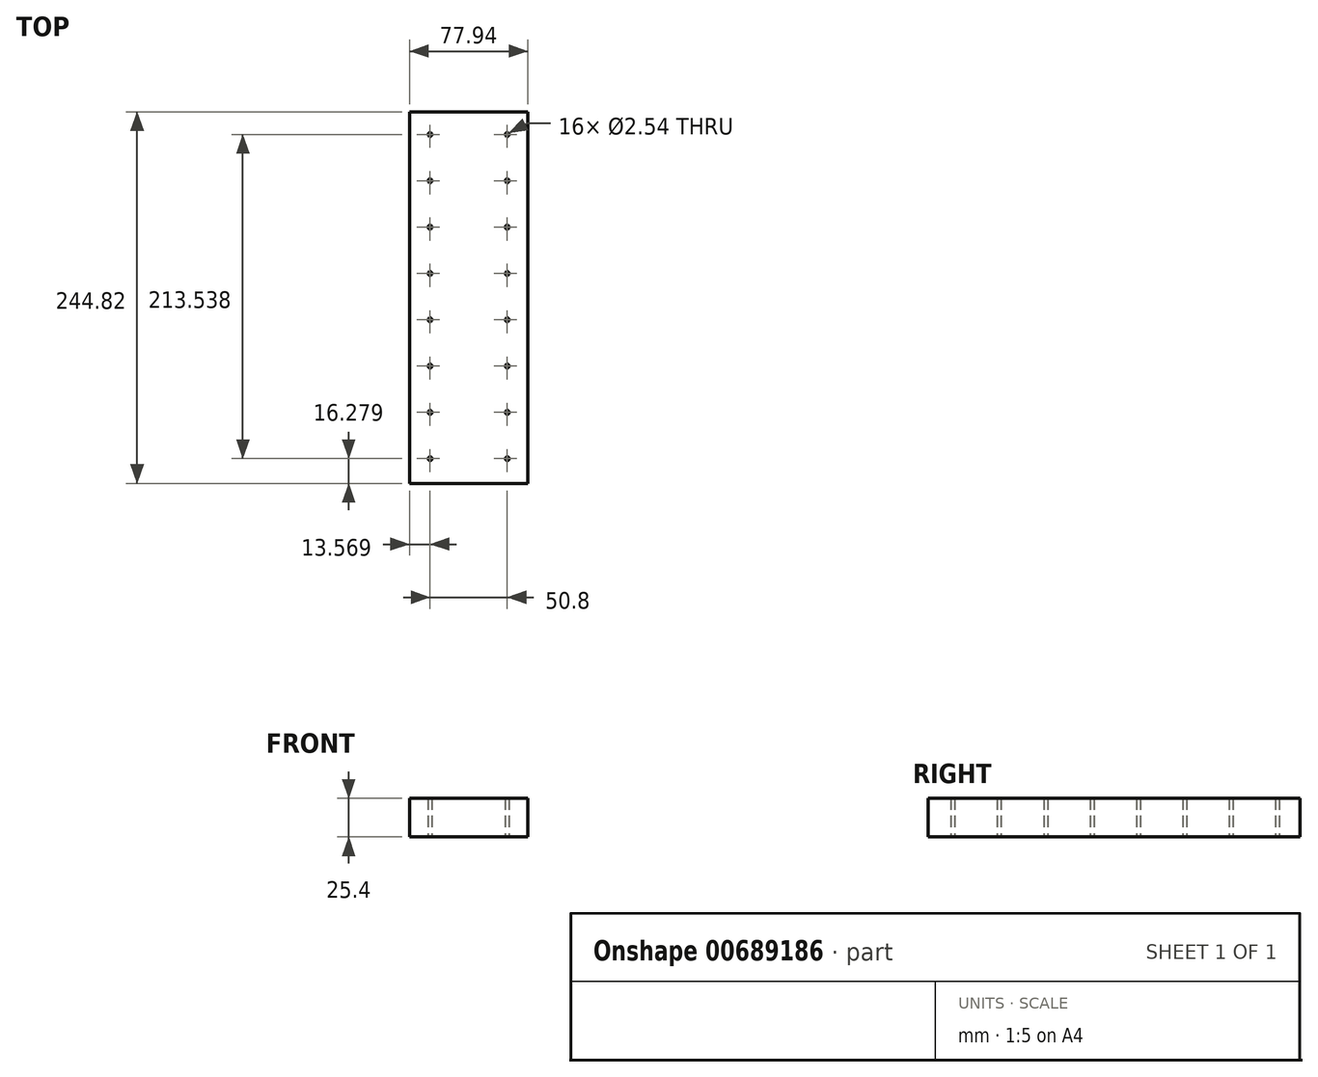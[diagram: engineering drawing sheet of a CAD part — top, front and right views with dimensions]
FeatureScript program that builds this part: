
annotation { "Feature Type Name" : "Feature", "Feature Type Description" : "" }
export const myFeature = defineFeature(function(context is Context, id is Id, definition is map)
    precondition{}
    {
        {
            var Q0;
            Q0=qCreatedBy(makeId("Top.planeOp"),FACE);
            var sketch = newSketch(context, id + "F0", { "sketchPlane" : qUnion([Q0])});
            skLineSegment(sketch, "E0", {"start": v(-47.84, 27.19) * mm, "end": v(2.96, 27.19) * mm, "construction": true});
            skCircle(sketch, "E1", {"center": v(-47.84, 27.19) * mm, "radius": 1.27 * mm});
            skCircle(sketch, "E2", {"center": v(2.96, 27.19) * mm, "radius": 1.27 * mm});
            skLineSegment(sketch, "E3.0.1.0", {"start": v(-47.84, -3.32) * mm, "end": v(2.96, -3.32) * mm, "construction": true});
            skCircle(sketch, "E3.0.1.1", {"center": v(-47.84, -3.32) * mm, "radius": 1.27 * mm});
            skCircle(sketch, "E3.0.1.2", {"center": v(2.96, -3.32) * mm, "radius": 1.27 * mm});
            skLineSegment(sketch, "E3.0.2.0", {"start": v(-47.84, -33.82) * mm, "end": v(2.96, -33.82) * mm, "construction": true});
            skCircle(sketch, "E3.0.2.1", {"center": v(-47.84, -33.82) * mm, "radius": 1.27 * mm});
            skCircle(sketch, "E3.0.2.2", {"center": v(2.96, -33.82) * mm, "radius": 1.27 * mm});
            skLineSegment(sketch, "E3.direction1", {"start": v(-47.84, 27.19) * mm, "end": v(-22.44, 27.19) * mm, "construction": true});
            skLineSegment(sketch, "E3.direction2", {"start": v(-47.84, 27.19) * mm, "end": v(-47.84, -3.32) * mm, "construction": true});
            skLineSegment(sketch, "E4.0.0.3", {"start": v(-47.84, -64.33) * mm, "end": v(2.96, -64.33) * mm, "construction": true});
            skCircle(sketch, "E4.3.0.3", {"center": v(-47.84, -64.33) * mm, "radius": 1.27 * mm});
            skCircle(sketch, "E4.5.0.3", {"center": v(2.96, -64.33) * mm, "radius": 1.27 * mm});
            skLineSegment(sketch, "E4.0.0.4", {"start": v(-47.84, -94.83) * mm, "end": v(2.96, -94.83) * mm, "construction": true});
            skCircle(sketch, "E4.3.0.4", {"center": v(-47.84, -94.83) * mm, "radius": 1.27 * mm});
            skCircle(sketch, "E4.5.0.4", {"center": v(2.96, -94.83) * mm, "radius": 1.27 * mm});
            skLineSegment(sketch, "E4.0.0.5", {"start": v(-47.84, -125.34) * mm, "end": v(2.96, -125.34) * mm, "construction": true});
            skCircle(sketch, "E4.3.0.5", {"center": v(-47.84, -125.34) * mm, "radius": 1.27 * mm});
            skCircle(sketch, "E4.5.0.5", {"center": v(2.96, -125.34) * mm, "radius": 1.27 * mm});
            skLineSegment(sketch, "E4.0.0.6", {"start": v(-47.84, -155.85) * mm, "end": v(2.96, -155.85) * mm, "construction": true});
            skCircle(sketch, "E4.3.0.6", {"center": v(-47.84, -155.85) * mm, "radius": 1.27 * mm});
            skCircle(sketch, "E4.5.0.6", {"center": v(2.96, -155.85) * mm, "radius": 1.27 * mm});
            skLineSegment(sketch, "E4.0.0.7", {"start": v(-47.84, -186.35) * mm, "end": v(2.96, -186.35) * mm, "construction": true});
            skCircle(sketch, "E4.3.0.7", {"center": v(-47.84, -186.35) * mm, "radius": 1.27 * mm});
            skCircle(sketch, "E4.5.0.7", {"center": v(2.96, -186.35) * mm, "radius": 1.27 * mm});
            skLineSegment(sketch, "E5.bottom", {"start": v(-61.4, 42.19) * mm, "end": v(16.53, 42.19) * mm, "construction": true});
            skLineSegment(sketch, "E5.top", {"start": v(-61.4, 12.19) * mm, "end": v(16.53, 12.19) * mm, "construction": true});
            skLineSegment(sketch, "E5.left", {"start": v(-61.4, 42.19) * mm, "end": v(-61.4, 12.19) * mm, "construction": true});
            skLineSegment(sketch, "E5.right", {"start": v(16.53, 42.19) * mm, "end": v(16.53, 12.19) * mm, "construction": true});
            skPoint(sketch, "E5.middle", {"position": v(-22.44, 27.19) * mm});
            skLineSegment(sketch, "E6.bottom", {"start": v(-61.4, 11.68) * mm, "end": v(16.53, 11.68) * mm, "construction": true});
            skLineSegment(sketch, "E6.top", {"start": v(-61.4, -18.32) * mm, "end": v(16.53, -18.32) * mm, "construction": true});
            skLineSegment(sketch, "E6.left", {"start": v(-61.4, 11.68) * mm, "end": v(-61.4, -18.32) * mm, "construction": true});
            skLineSegment(sketch, "E6.right", {"start": v(16.53, 11.68) * mm, "end": v(16.53, -18.32) * mm, "construction": true});
            skPoint(sketch, "E6.middle", {"position": v(-22.44, -3.32) * mm});
            skLineSegment(sketch, "E7.bottom", {"start": v(-61.4, 42.19) * mm, "end": v(16.53, 42.19) * mm});
            skLineSegment(sketch, "E7.top", {"start": v(-61.4, -202.63) * mm, "end": v(16.53, -202.63) * mm});
            skLineSegment(sketch, "E7.left", {"start": v(-61.4, 42.19) * mm, "end": v(-61.4, -202.63) * mm});
            skLineSegment(sketch, "E7.right", {"start": v(16.53, 42.19) * mm, "end": v(16.53, -202.63) * mm});
            skSolve(sketch);
        }
        {
            var Q0;
            Q0=makeQuery(id+"F0.imprint","IMPRINT",FACE,{"disambiguationData":[TD([[makeQuery(id+"F0.imprint","IMPRINT",EDGE,{"derivedFrom":sQuery(id+"F0.wireOp",EDGE,"E1")}),-1.0]])]});
            extrude(context, id + "F1", {"entities" : qUnion([Q0]), "depth" : 25.4 * mm, "offsetDistance" : 25.4 * mm});
        }
    });
